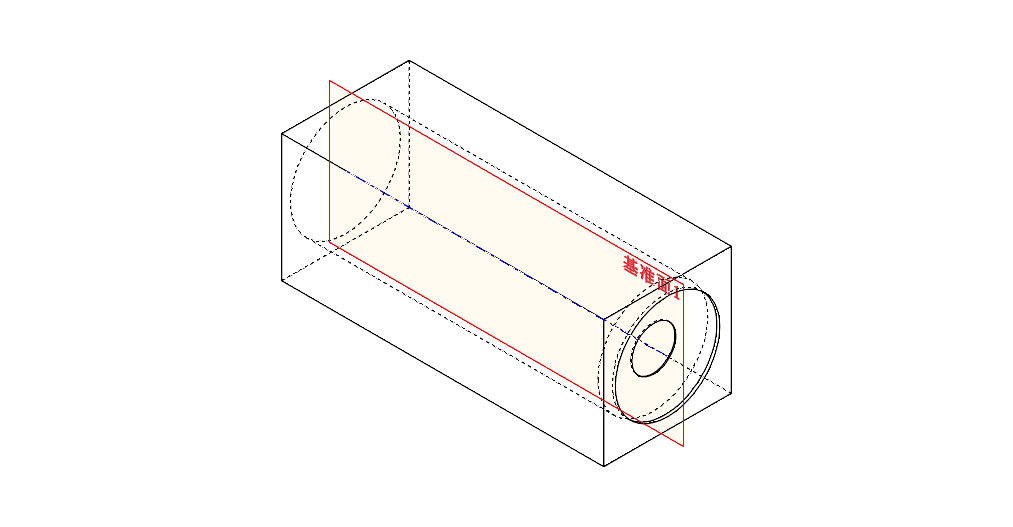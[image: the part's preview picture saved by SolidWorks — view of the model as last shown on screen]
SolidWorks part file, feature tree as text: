
SOLIDWORKS PART (.sldprt)
format: sldprt  version: not decoded by parser v0  size: 211,968 bytes
history: native  units: mm
features: plane x4, sketch x3, material x1, extrude x1, cut_extrude x1, cut_revolve x1 (+10 scaffold rows collapsed)
feature tree (21):
  scaffold x10  (default folders/planes/origin — collapsed)
  material  "材质 <未指定>"
  plane  "前视"
  plane  "上视"
  plane  "右视"
  sketch  "草图1"  dims[D1=130.5mm]
  extrude  "凸台-拉伸1"  Depth=330mm
  sketch  "草图8"  dims[D1=~51.28864mm]
  cut_extrude  "切除-拉伸2"  Depth=315mm
  plane  "基准面1"  Offset=65.25mm
  sketch  "草图26"  dims[D1=22.5mm D2=1.0mm D3=3.0mm]
  cut_revolve  "切除-旋转3"  Angle=360deg
decode coverage: 6 of 6 modeling features carry decoded parameters
note: ~ marks probable driven/reference dimensions
note: suppression state not decoded; provenance and decode notes live in map.json
